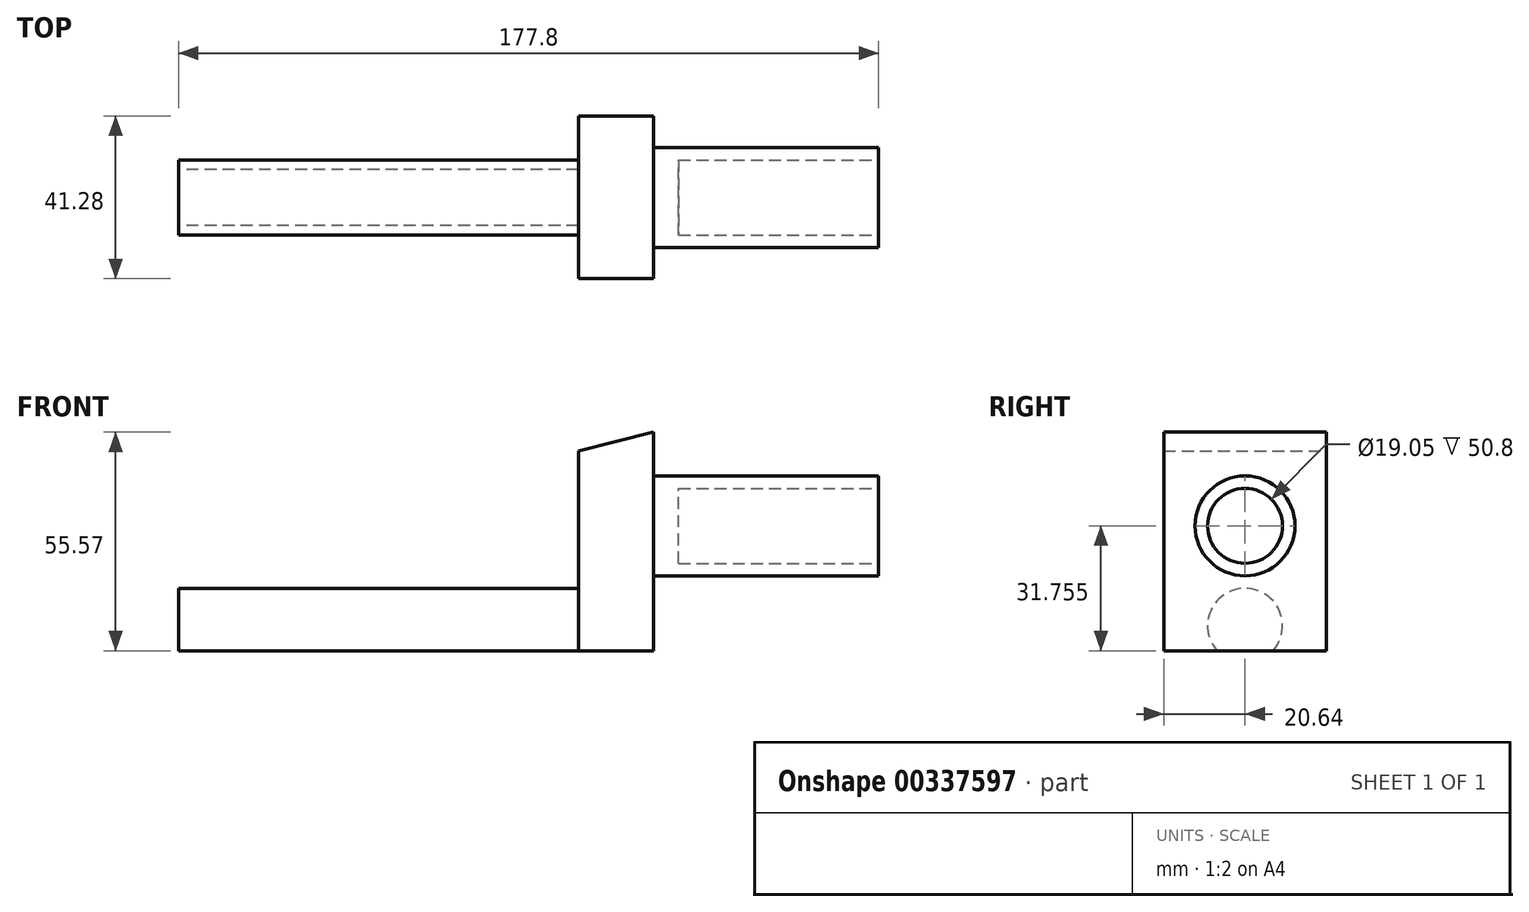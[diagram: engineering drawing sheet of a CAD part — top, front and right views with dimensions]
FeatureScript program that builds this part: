
annotation { "Feature Type Name" : "Feature", "Feature Type Description" : "" }
export const myFeature = defineFeature(function(context is Context, id is Id, definition is map)
    precondition{}
    {
        {
            var Q0;
            Q0=qCreatedBy(makeId("Front.planeOp"),FACE);
            var sketch = newSketch(context, id + "F0", { "sketchPlane" : qUnion([Q0])});
            skLineSegment(sketch, "E0.top", {"start": v(101.6, -34.93) * mm, "end": v(-101.6, -34.93) * mm});
            skLineSegment(sketch, "E0.left", {"start": v(101.6, 34.93) * mm, "end": v(101.6, -34.93) * mm});
            skLineSegment(sketch, "E0.right", {"start": v(-101.6, -15.88) * mm, "end": v(-101.6, -34.93) * mm});
            skPoint(sketch, "E0.middle", {"position": v(0, 0) * mm});
            skLineSegment(sketch, "E1", {"start": v(-101.6, -15.88) * mm, "end": v(101.6, 34.93) * mm});
            skPoint(sketch, "E2.orphan", {"position": v(-101.6, 34.93) * mm});
            skSolve(sketch);
        }
        {
            var Q0;
            Q0 = qSketchRegion(id + "F0", true);
            extrude(context, id + "F1", {"entities" : qUnion([Q0]), "endBound" : BoundingType.SYMMETRIC, "depth" : 41.27 * mm});
        }
        {
            var Q0;
            Q0=makeQuery(id+"F1.opExtrude","SWEPT_FACE",FACE,{"disambiguationData":[OSD([sQuery(id+"F0.wireOp",EDGE,"E0.left")])]});
            var sketch = newSketch(context, id + "F2", { "sketchPlane" : qUnion([Q0])});
            skCircle(sketch, "E3", {"center": v(0, -3.17) * mm, "radius": 9.53 * mm});
            skSolve(sketch);
        }
        {
            var Q0;
            Q0 = qSketchRegion(id + "F2", true);
            extrude(context, id + "F3", {"entities" : qUnion([Q0]), "operationType" : NewBodyOperationType.REMOVE, "oppositeDirection" : true, "depth" : 50.8 * mm});
        }
        {
            var Q0;
            Q0=makeQuery(id+"F1.opExtrude","SWEPT_FACE",FACE,{"disambiguationData":[OSD([sQuery(id+"F0.wireOp",EDGE,"E0.right")])]});
            var sketch = newSketch(context, id + "F4", { "sketchPlane" : qUnion([Q0])});
            skPoint(sketch, "E4", {"position": v(0, -28.58) * mm});
            skArc(sketch, "E5", {"start": v(7.1, -34.93) * mm, "mid": v(0, -19.05) * mm, "end": v(-7.1, -34.93) * mm});
            skLineSegment(sketch, "E6", {"start": v(-7.1, -34.93) * mm, "end": v(7.1, -34.93) * mm});
            skSolve(sketch);
        }
        {
            var Q0;
            {var subQ3=sQuery(id+"F4.wireOp",EDGE,"OsH91NJB-KZNr-D7xO-vqEM-75ufx17OOHr1");Q0=makeQuery(id+"F4.imprint","IMPRINT",FACE,{"disambiguationData":[TD([[makeQuery(id+"F4.imprint","IMPRINT",EDGE,{"derivedFrom":subQ3}),-1.0]])]});}
            var Q1;
            {var subQ3=sQuery(id+"F4.wireOp",EDGE,"E5");Q1=makeQuery(id+"F4.imprint","IMPRINT",FACE,{"disambiguationData":[TD([[makeQuery(id+"F4.imprint","IMPRINT",EDGE,{"derivedFrom":subQ3}),-1.0]])]});}
            extrude(context, id + "F5", {"entities" : qUnion([Q0, Q1]), "operationType" : NewBodyOperationType.REMOVE, "oppositeDirection" : true, "depth" : 127 * mm});
        }
        {
            var Q0;
            Q0=makeQuery(id+"F1.opExtrude","CAP_FACE",FACE,{"disambiguationData":[OSD([sQuery(id+"F0.wireOp",EDGE,"E0.top"),sQuery(id+"F0.wireOp",EDGE,"E0.left"),sQuery(id+"F0.wireOp",EDGE,"E0.right"),sQuery(id+"F0.wireOp",EDGE,"E1")])],"isStart":true});
            var sketch = newSketch(context, id + "F6", { "sketchPlane" : qUnion([Q0])});
            skLineSegment(sketch, "E7", {"start": v(-25.4, -15.88) * mm, "end": v(-25.4, 15.88) * mm});
            skLineSegment(sketch, "E8", {"start": v(-25.4, 15.87) * mm, "end": v(101.6, -15.88) * mm});
            skLineSegment(sketch, "E9", {"start": v(101.6, -15.88) * mm, "end": v(-25.4, -15.88) * mm});
            skSolve(sketch);
        }
        {
            var Q0;
            Q0 = qSketchRegion(id + "F6", true);
            extrude(context, id + "F7", {"entities" : qUnion([Q0]), "operationType" : NewBodyOperationType.REMOVE, "endBound" : BoundingType.THROUGH_ALL, "oppositeDirection" : true, "depth" : 25.4 * mm});
        }
        {
            var Q0;
            Q0=makeQuery(id+"F1.opExtrude","SWEPT_FACE",FACE,{"disambiguationData":[OSD([sQuery(id+"F0.wireOp",EDGE,"E0.left")])]});
            var sketch = newSketch(context, id + "F8", { "sketchPlane" : qUnion([Q0])});
            skCircle(sketch, "E10", {"center": v(0, -3.17) * mm, "radius": 12.7 * mm});
            skSolve(sketch);
        }
        {
            var Q0;
            Q0=makeQuery(id+"F8.imprint","IMPRINT",FACE,{"disambiguationData":[TD([[makeQuery(id+"F8.imprint","IMPRINT",EDGE,{"derivedFrom":sQuery(id+"F8.wireOp",EDGE,"E10")}),-1.0]])]});
            extrude(context, id + "F9", {"entities" : qUnion([Q0]), "operationType" : NewBodyOperationType.REMOVE, "oppositeDirection" : true, "depth" : 57.15 * mm});
        }
        {
            var Q0;
            Q0=qCreatedBy(makeId("Top.planeOp"),FACE);
            var sketch = newSketch(context, id + "F10", { "sketchPlane" : qUnion([Q0])});
            skLineSegment(sketch, "E11.bottom", {"start": v(-101.6, -18.1) * mm, "end": v(-76.2, -18.1) * mm});
            skLineSegment(sketch, "E11.top", {"start": v(-101.6, 14.7) * mm, "end": v(-76.2, 14.7) * mm});
            skLineSegment(sketch, "E11.left", {"start": v(-101.6, -18.1) * mm, "end": v(-101.6, 14.7) * mm});
            skLineSegment(sketch, "E11.right", {"start": v(-76.2, -18.1) * mm, "end": v(-76.2, 14.7) * mm});
            skSolve(sketch);
        }
        {
            var Q0;
            Q0=makeQuery(id+"F10.imprint","IMPRINT",FACE,{"disambiguationData":[TD([[makeQuery(id+"F10.imprint","IMPRINT",EDGE,{"derivedFrom":sQuery(id+"F10.wireOp",EDGE,"E11.bottom")}),1.0]])]});
            extrude(context, id + "F11", {"entities" : qUnion([Q0]), "operationType" : NewBodyOperationType.REMOVE, "endBound" : BoundingType.THROUGH_ALL, "oppositeDirection" : true, "depth" : 25.4 * mm});
        }
    });
